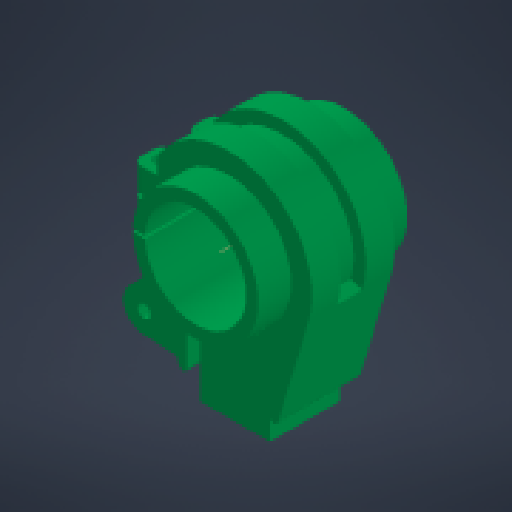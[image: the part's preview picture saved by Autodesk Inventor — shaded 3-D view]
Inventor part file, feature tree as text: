
AUTODESK INVENTOR PART (.ipt)
format: ipt  version: 2024 (Build 280153000, 153)  size: 448,512 bytes
history: native  units: mm
features: other x16, sketch x14, extrude x11, fillet x4, mirror x3, projected_geometry x2, reference x2, shell x1, sweep x1
ambient origin geometry x8: Origin, YZ Plane, XZ Plane, XY Plane, X Axis, Y Axis, Z Axis, Center Point
bodies: Body1 (feature_tree)
feature tree (54):
  other  "Твердое тело1"
  extrude  "Выдавливание1"  Depth=20.0mm
  shell  "Оболочка1"  Thickness=1.5mm
  extrude  "Выдавливание2"  Depth=20.0mm TaperAngle=0.0deg
  other  "РабПлоскость1"
  extrude  "Выдавливание4"  Depth=4.0mm
  sketch  "Эскиз8"
  other  "РабПлоскость3"
  sweep  "Сдвиг1"
  other  "РабОсь1"
  other  "РабПлоскость4"
  fillet  "Сопряжение2"  Radius=5.0mm
  other  "РабПлоскость5"
  other  "РабПлоскость6"
  other  "РабПлоскость7"
  other  "РабПлоскость8"
  extrude  "Выдавливание18"  Depth=20.0mm TaperAngle=0.0deg
  extrude  "Выдавливание19"  Depth=20.2mm
  extrude  "Выдавливание20"  Depth=24.4mm
  mirror  "Зеркальное отражение7"
  other  "Непосредственное редактирование3"
  fillet  "Сопряжение9"  Radius=8.0mm
  fillet  "Сопряжение10"  [1 undecoded]
  other  "Непосредственное редактирование4"
  extrude  "Выдавливание22"  Depth=3.0mm
  mirror  "Зеркальное отражение8"
  extrude  "Выдавливание23"  Depth=6.0mm
  extrude  "Выдавливание24"  Depth=1.0mm
  extrude  "Выдавливание25"  Depth=6.0mm
  mirror  "Зеркальное отражение9"
  extrude  "Выдавливание26"  Depth=16.25mm TaperAngle=0.0deg
  fillet  "Сопряжение11"  Radius=3.0mm
  sketch  "Эскиз1"
  sketch  "Эскиз2"
  projected_geometry  "Спроецированная петля1"
  sketch  "Эскиз5"
  reference  "Ссылка3"
  reference  "Ссылка4"
  sketch  "Эскиз10"
  sketch  "3D эскиз1"
  sketch  "Эскиз32"
  sketch  "Эскиз33"
  sketch  "Эскиз35"
  sketch  "Эскиз37"
  sketch  "Эскиз39"
  sketch  "Эскиз40"
  projected_geometry  "Спроецированная петля3"
  sketch  "Эскиз41"
  sketch  "Эскиз42"
  parser-record x1  (decoder bookkeeping rows leaked as tree rows — omitted from the tree; the rows remain in map.json)
  other  "arm_assembly.iam"
  other  "arm:1"
  other  "Перенос3"
  other  "Перенос4"
note: 1 required parameter value undecoded (feature->parameter linkage not recoverable at this tier; creation-order binding heuristic only, values carry confidence <= 0.55)
note: 1 file-system path scrubbed to <path> (originals preserved in map.json)
